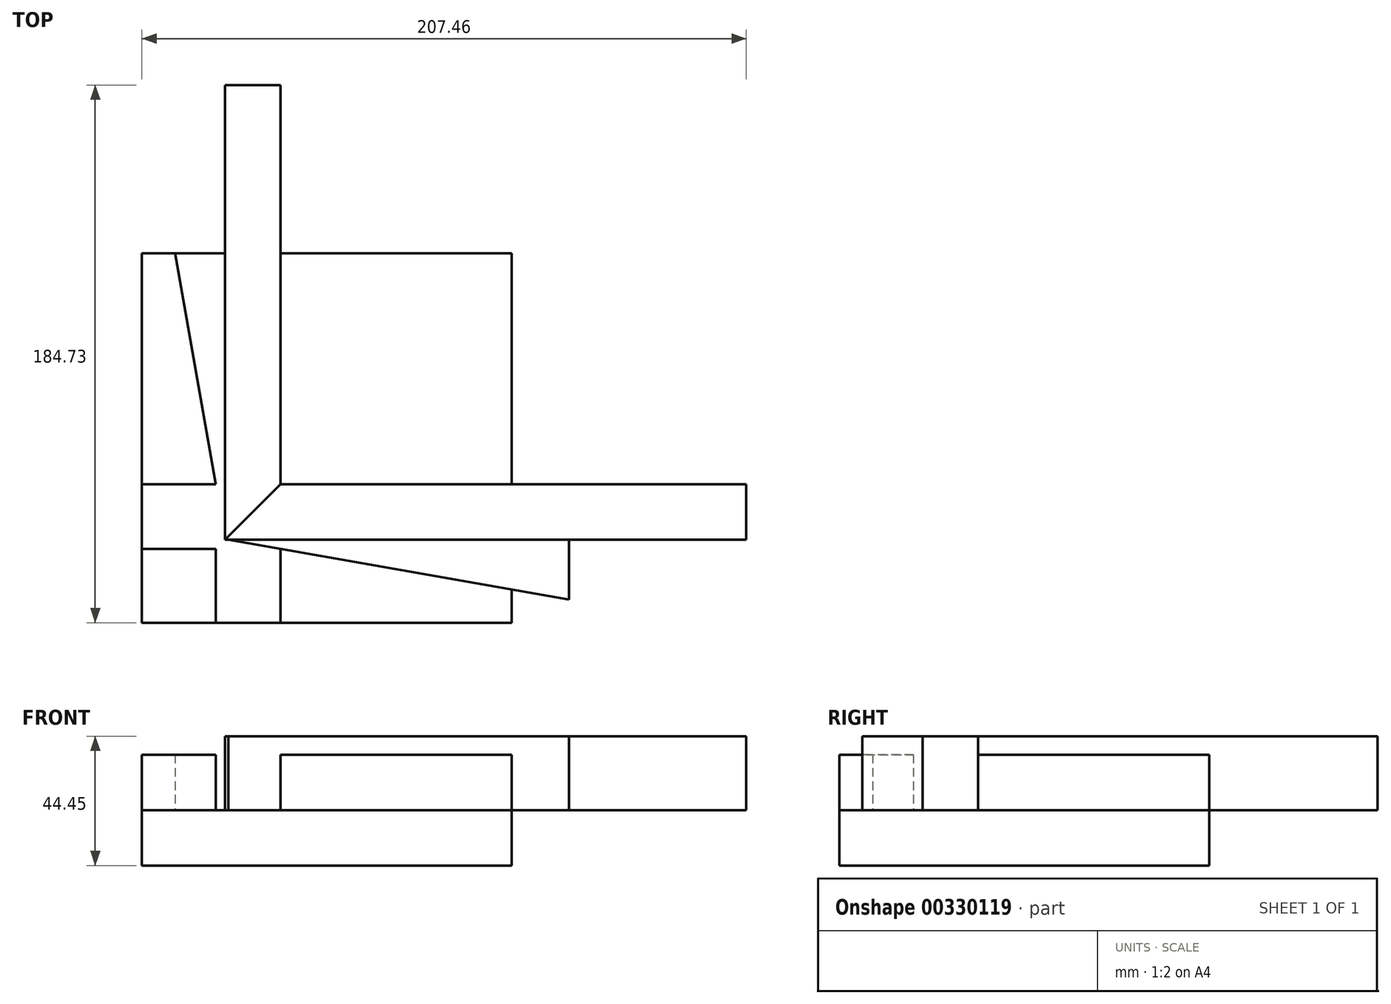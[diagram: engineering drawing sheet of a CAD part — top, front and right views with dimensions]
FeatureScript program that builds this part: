
annotation { "Feature Type Name" : "Feature", "Feature Type Description" : "" }
export const myFeature = defineFeature(function(context is Context, id is Id, definition is map)
    precondition{}
    {
        {
            var Q0;
            Q0=qCreatedBy(makeId("Top.planeOp"),FACE);
            var sketch = newSketch(context, id + "F0", { "sketchPlane" : qUnion([Q0])});
            skLineSegment(sketch, "E0.bottom", {"start": v(63.5, 63.5) * mm, "end": v(-63.5, 63.5) * mm});
            skLineSegment(sketch, "E0.top", {"start": v(63.5, -63.5) * mm, "end": v(-63.5, -63.5) * mm});
            skLineSegment(sketch, "E0.left", {"start": v(63.5, 63.5) * mm, "end": v(63.5, -63.5) * mm});
            skLineSegment(sketch, "E0.right", {"start": v(-63.5, 63.5) * mm, "end": v(-63.5, -63.5) * mm});
            skPoint(sketch, "E0.middle", {"position": v(0, 0) * mm});
            skSolve(sketch);
        }
        {
            var Q0;
            Q0=makeQuery(id+"F0.imprint","IMPRINT",FACE,{"disambiguationData":[TD([[makeQuery(id+"F0.imprint","IMPRINT",EDGE,{"derivedFrom":sQuery(id+"F0.wireOp",EDGE,"E0.bottom")}),1.0]])]});
            extrude(context, id + "F1", {"entities" : qUnion([Q0]), "depth" : 19.05 * mm});
        }
        {
            var Q0;
            Q0=makeQuery(id+"F1.opExtrude","CAP_FACE",FACE,{"disambiguationData":[OSD([sQuery(id+"F0.wireOp",EDGE,"E0.bottom"),sQuery(id+"F0.wireOp",EDGE,"E0.top"),sQuery(id+"F0.wireOp",EDGE,"E0.left"),sQuery(id+"F0.wireOp",EDGE,"E0.right")])],"isStart":false});
            var sketch = newSketch(context, id + "F2", { "sketchPlane" : qUnion([Q0])});
            skLineSegment(sketch, "E1", {"start": v(-15.87, -63.5) * mm, "end": v(-15.87, -38.1) * mm});
            skLineSegment(sketch, "E2", {"start": v(-15.87, -38.1) * mm, "end": v(63.5, -52.1) * mm});
            skLineSegment(sketch, "E3", {"start": v(63.5, -52.1) * mm, "end": v(63.5, -63.5) * mm});
            skLineSegment(sketch, "E4", {"start": v(63.5, -63.5) * mm, "end": v(-15.87, -63.5) * mm});
            skLineSegment(sketch, "E5", {"start": v(-63.5, -15.87) * mm, "end": v(-38.1, -15.87) * mm});
            skLineSegment(sketch, "E6", {"start": v(-38.1, -15.87) * mm, "end": v(-52.1, 63.5) * mm});
            skLineSegment(sketch, "E7", {"start": v(-52.1, 63.5) * mm, "end": v(-63.5, 63.5) * mm});
            skLineSegment(sketch, "E8", {"start": v(-63.5, 63.5) * mm, "end": v(-63.5, -15.87) * mm});
            skLineSegment(sketch, "E9.bottom", {"start": v(-63.5, -63.5) * mm, "end": v(-38.1, -63.5) * mm});
            skLineSegment(sketch, "E9.top", {"start": v(-63.5, -38.1) * mm, "end": v(-38.1, -38.1) * mm});
            skLineSegment(sketch, "E9.left", {"start": v(-63.5, -63.5) * mm, "end": v(-63.5, -38.1) * mm});
            skLineSegment(sketch, "E9.right", {"start": v(-38.1, -63.5) * mm, "end": v(-38.1, -38.1) * mm});
            skLineSegment(sketch, "E10.bottom", {"start": v(63.5, 63.5) * mm, "end": v(-15.88, 63.5) * mm});
            skLineSegment(sketch, "E10.top", {"start": v(63.5, -15.87) * mm, "end": v(-15.87, -15.87) * mm});
            skLineSegment(sketch, "E10.left", {"start": v(63.5, 63.5) * mm, "end": v(63.5, -15.87) * mm});
            skLineSegment(sketch, "E10.right", {"start": v(-15.88, 63.5) * mm, "end": v(-15.87, -15.87) * mm});
            skSolve(sketch);
        }
        {
            var Q0;
            Q0=makeQuery(id+"F2.imprint","IMPRINT",FACE,{"disambiguationData":[TD([[makeQuery(id+"F2.imprint","IMPRINT",EDGE,{"derivedFrom":sQuery(id+"F2.wireOp",EDGE,"E5")}),1.0]])]});
            var Q1;
            Q1=makeQuery(id+"F2.imprint","IMPRINT",FACE,{"disambiguationData":[TD([[makeQuery(id+"F2.imprint","IMPRINT",EDGE,{"derivedFrom":sQuery(id+"F2.wireOp",EDGE,"E9.bottom")}),-1.0]])]});
            var Q2;
            Q2=makeQuery(id+"F2.imprint","IMPRINT",FACE,{"disambiguationData":[TD([[makeQuery(id+"F2.imprint","IMPRINT",EDGE,{"derivedFrom":sQuery(id+"F2.wireOp",EDGE,"E1")}),-1.0]])]});
            var Q3;
            Q3=makeQuery(id+"F2.imprint","IMPRINT",FACE,{"disambiguationData":[TD([[makeQuery(id+"F2.imprint","IMPRINT",EDGE,{"derivedFrom":sQuery(id+"F2.wireOp",EDGE,"E10.bottom")}),1.0]])]});
            extrude(context, id + "F3", {"entities" : qUnion([Q0, Q1, Q2, Q3]), "depth" : 19.05 * mm});
        }
        {
            var Q0;
            Q0=makeQuery(id+"F1.opExtrude","CAP_FACE",FACE,{"disambiguationData":[OSD([sQuery(id+"F0.wireOp",EDGE,"E0.bottom"),sQuery(id+"F0.wireOp",EDGE,"E0.top"),sQuery(id+"F0.wireOp",EDGE,"E0.left"),sQuery(id+"F0.wireOp",EDGE,"E0.right")])],"isStart":false});
            var sketch = newSketch(context, id + "F4", { "sketchPlane" : qUnion([Q0])});
            skLineSegment(sketch, "E11", {"start": v(83.18, -34.92) * mm, "end": v(-33.88, -34.92) * mm});
            skLineSegment(sketch, "E12", {"start": v(-33.88, -34.92) * mm, "end": v(83.18, -55.57) * mm});
            skLineSegment(sketch, "E13", {"start": v(83.18, -55.57) * mm, "end": v(83.18, -34.92) * mm});
            skSolve(sketch);
        }
        {
            var Q0;
            Q0 = qSketchRegion(id + "F4", true);
            extrude(context, id + "F5", {"entities" : qUnion([Q0]), "depth" : 25.4 * mm});
        }
        {
            var Q0;
            Q0=makeQuery(id+"F1.opExtrude","CAP_FACE",FACE,{"disambiguationData":[OSD([sQuery(id+"F0.wireOp",EDGE,"E0.bottom"),sQuery(id+"F0.wireOp",EDGE,"E0.top"),sQuery(id+"F0.wireOp",EDGE,"E0.left"),sQuery(id+"F0.wireOp",EDGE,"E0.right")])],"isStart":false});
            var sketch = newSketch(context, id + "F6", { "sketchPlane" : qUnion([Q0])});
            skLineSegment(sketch, "E14", {"start": v(-34.92, -34.92) * mm, "end": v(143.96, -34.92) * mm});
            skLineSegment(sketch, "E15", {"start": v(143.96, -34.92) * mm, "end": v(143.96, -15.87) * mm});
            skLineSegment(sketch, "E16", {"start": v(143.96, -15.87) * mm, "end": v(-15.88, -15.87) * mm});
            skLineSegment(sketch, "E17", {"start": v(-15.88, -15.87) * mm, "end": v(-34.92, -34.92) * mm});
            skLineSegment(sketch, "E18", {"start": v(-34.92, -34.92) * mm, "end": v(-34.93, 121.23) * mm});
            skLineSegment(sketch, "E19", {"start": v(-34.93, 121.23) * mm, "end": v(-15.88, 121.23) * mm});
            skLineSegment(sketch, "E20", {"start": v(-15.88, 121.23) * mm, "end": v(-15.88, -15.87) * mm});
            skSolve(sketch);
        }
        {
            var Q0;
            {var subQ0=sQuery(id+"F6.wireOp",EDGE,"E17");Q0=makeQuery(id+"F6.imprint","IMPRINT",FACE,{"disambiguationData":[TD([[makeQuery(id+"F6.imprint","IMPRINT",EDGE,{"derivedFrom":subQ0}),-1.0]])]});}
            var Q1;
            {var subQ0=sQuery(id+"F6.wireOp",EDGE,"E19");Q1=makeQuery(id+"F6.imprint","IMPRINT",FACE,{"disambiguationData":[TD([[makeQuery(id+"F6.imprint","IMPRINT",EDGE,{"derivedFrom":subQ0}),-1.0]])]});}
            extrude(context, id + "F7", {"entities" : qUnion([Q0, Q1]), "depth" : 25.4 * mm});
        }
        {
            var Q0;
            {var subQ0=sQuery(id+"F6.wireOp",EDGE,"E17");Q0=makeQuery(id+"F6.imprint","IMPRINT",FACE,{"disambiguationData":[TD([[makeQuery(id+"F6.imprint","IMPRINT",EDGE,{"derivedFrom":subQ0}),1.0]])]});}
            var Q1;
            {var subQ0=sQuery(id+"F6.wireOp",EDGE,"E15");Q1=makeQuery(id+"F6.imprint","IMPRINT",FACE,{"disambiguationData":[TD([[makeQuery(id+"F6.imprint","IMPRINT",EDGE,{"derivedFrom":subQ0}),1.0]])]});}
            extrude(context, id + "F8", {"entities" : qUnion([Q0, Q1]), "depth" : 25.4 * mm});
        }
    });
